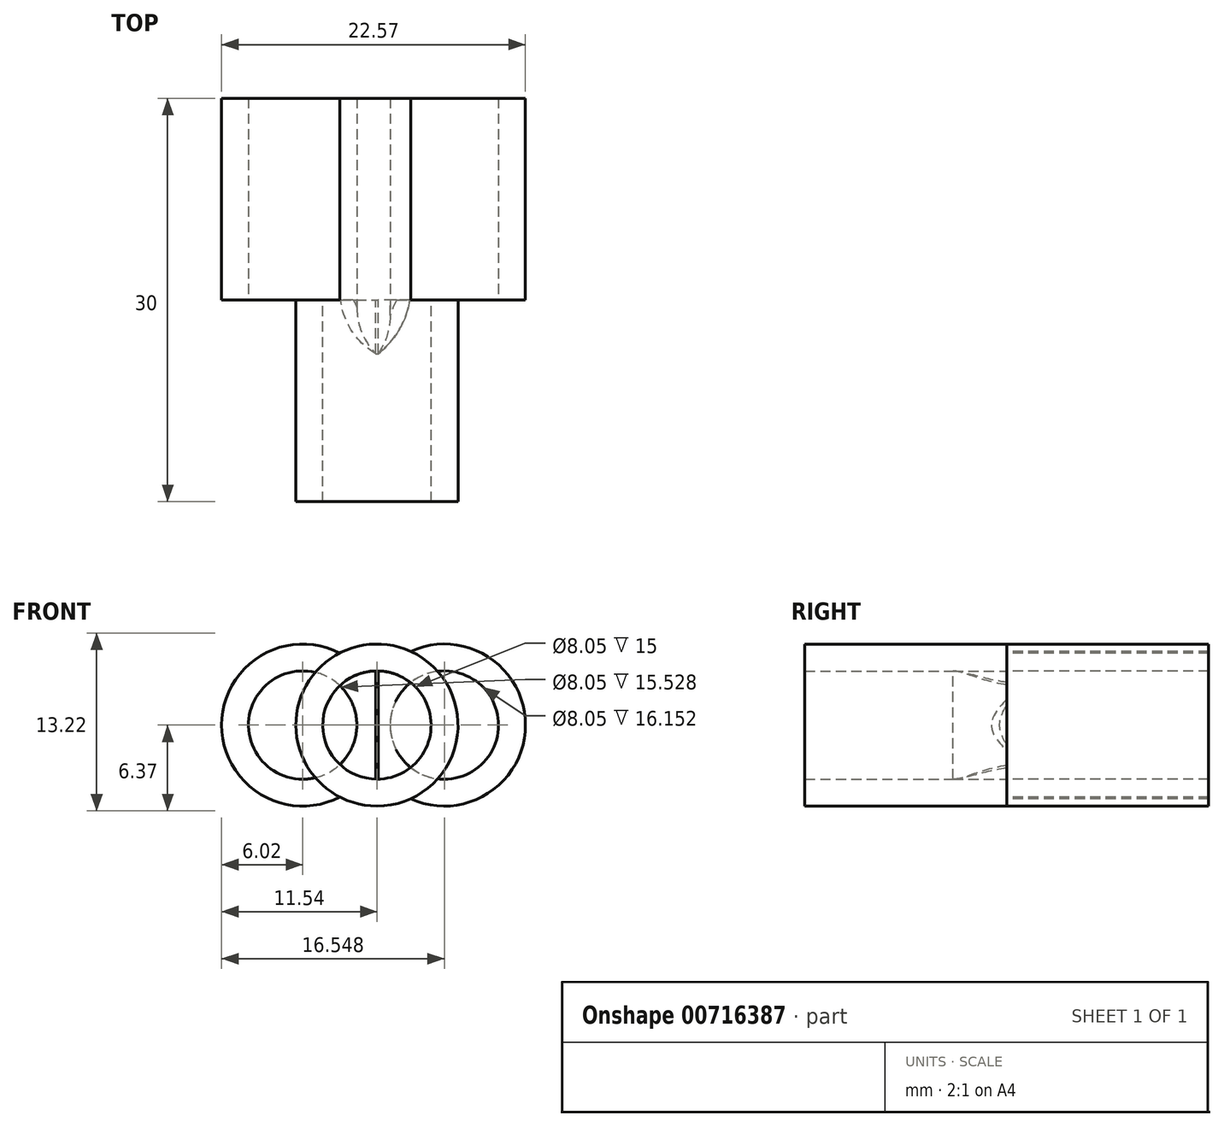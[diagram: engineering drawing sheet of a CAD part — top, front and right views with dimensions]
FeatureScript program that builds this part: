
annotation { "Feature Type Name" : "Feature", "Feature Type Description" : "" }
export const myFeature = defineFeature(function(context is Context, id is Id, definition is map)
    precondition{}
    {
        {
            var Q0;
            Q0=qCreatedBy(makeId("Front.planeOp"),FACE);
            var sketch = newSketch(context, id + "F0", { "sketchPlane" : qUnion([Q0])});
            skCircle(sketch, "E0", {"center": v(5.52, 0) * mm, "radius": 4.03 * mm});
            skCircle(sketch, "E1", {"center": v(5.52, 0) * mm, "radius": 6.03 * mm});
            skSolve(sketch);
        }
        {
            var Q0;
            Q0 = qSketchRegion(id + "F0", true);
            extrude(context, id + "F1", {"entities" : qUnion([Q0]), "depth" : 15 * mm, "offsetDistance" : 25 * mm});
        }
        {
            var Q0;
            Q0=qCreatedBy(makeId("Front.planeOp"),FACE);
            var sketch = newSketch(context, id + "F2", { "sketchPlane" : qUnion([Q0])});
            skCircle(sketch, "E2", {"center": v(10.53, 0) * mm, "radius": 6.03 * mm});
            skCircle(sketch, "E3", {"center": v(0, 0) * mm, "radius": 6.03 * mm});
            skCircle(sketch, "E4", {"center": v(10.53, 0) * mm, "radius": 4.03 * mm});
            skCircle(sketch, "E5", {"center": v(0, 0) * mm, "radius": 4.03 * mm});
            skSolve(sketch);
        }
        {
            var Q0;
            Q0=makeQuery(id+"F2.imprint","IMPRINT",FACE,{"disambiguationData":[TD([[makeQuery(id+"F2.imprint","IMPRINT",EDGE,{"derivedFrom":sQuery(id+"F2.wireOp",EDGE,"E5")}),-1.0]])]});
            var Q1;
            Q1=makeQuery(id+"F2.imprint","IMPRINT",FACE,{"disambiguationData":[TD([[makeQuery(id+"F2.imprint","IMPRINT",EDGE,{"derivedFrom":sQuery(id+"F2.wireOp",EDGE,"E4")}),-1.0]])]});
            extrude(context, id + "F3", {"entities" : qUnion([Q0, Q1]), "oppositeDirection" : true, "depth" : 15 * mm, "offsetDistance" : 25 * mm});
        }
        {
            var Q0;
            Q0=makeQuery(id+"F0.imprint","IMPRINT",FACE,{"disambiguationData":[TD([[makeQuery(id+"F0.imprint","IMPRINT",EDGE,{"derivedFrom":sQuery(id+"F0.wireOp",EDGE,"E0")}),1.0]])]});
            var sketch = newSketch(context, id + "F4", { "sketchPlane" : qUnion([Q0])});
            skArc(sketch, "E6.0", {"start": v(6.37, 4.36) * mm, "mid": v(7.15, 4.99) * mm, "end": v(8.02, 5.48) * mm});
            skArc(sketch, "E7.0", {"start": v(4.36, -4.16) * mm, "mid": v(6.03, 0) * mm, "end": v(4.36, 4.16) * mm});
            skArc(sketch, "E8.0", {"start": v(8.02, 5.48) * mm, "mid": v(5.38, 6.02) * mm, "end": v(2.76, 5.36) * mm});
            skArc(sketch, "E9.0", {"start": v(2.76, -5.36) * mm, "mid": v(6.03, 0) * mm, "end": v(2.76, 5.36) * mm});
            skArc(sketch, "E10.trimOffspring", {"start": v(2.76, -5.36) * mm, "mid": v(5.38, -6.02) * mm, "end": v(8.02, -5.48) * mm});
            skArc(sketch, "E11.0", {"start": v(5.26, 2.93) * mm, "mid": v(4.5, 0) * mm, "end": v(5.26, -2.93) * mm});
            skArc(sketch, "E12.0.0", {"start": v(5.26, 2.93) * mm, "mid": v(6.44, 4.43) * mm, "end": v(8.02, 5.48) * mm});
            skArc(sketch, "E12.0.1", {"start": v(5.26, -2.93) * mm, "mid": v(6.03, 0) * mm, "end": v(5.26, 2.93) * mm});
            skArc(sketch, "E13.0.1", {"start": v(5.26, -2.93) * mm, "mid": v(4.2, -4.33) * mm, "end": v(2.76, -5.36) * mm});
            skArc(sketch, "E14.trimOffspring", {"start": v(2.76, 5.36) * mm, "mid": v(4.2, 4.33) * mm, "end": v(5.26, 2.93) * mm});
            skArc(sketch, "E15.trimOffspring", {"start": v(8.02, -5.48) * mm, "mid": v(6.44, -4.43) * mm, "end": v(5.26, -2.93) * mm});
            skArc(sketch, "E16.trimOffspring", {"start": v(8.02, -5.48) * mm, "mid": v(7.15, -4.99) * mm, "end": v(6.37, -4.36) * mm});
            skSolve(sketch);
        }
        {
            var Q0;
            Q0 = qSketchRegion(id + "F4", true);
            extrude(context, id + "F5", {"entities" : qUnion([Q0]), "operationType" : NewBodyOperationType.ADD, "depth" : -15 * mm, "offsetDistance" : 25 * mm});
        }
        {
            var Q0;
            Q0=makeQuery(id+"F0.imprint","IMPRINT",FACE,{"disambiguationData":[TD([[makeQuery(id+"F0.imprint","IMPRINT",EDGE,{"derivedFrom":sQuery(id+"F0.wireOp",EDGE,"E0")}),1.0]])]});
            var sketch = newSketch(context, id + "F6", { "sketchPlane" : qUnion([Q0])});
            skArc(sketch, "E17.0", {"start": v(5.43, -4.02) * mm, "mid": v(5.52, -4.03) * mm, "end": v(5.61, -4.02) * mm});
            skPoint(sketch, "E18.0", {"position": v(5.61, 3.48) * mm});
            skArc(sketch, "E19.0.0", {"start": v(5.61, 4.02) * mm, "mid": v(5.1, 4) * mm, "end": v(4.58, 3.91) * mm});
            skPoint(sketch, "E20.0", {"position": v(5.61, -3.48) * mm});
            skPoint(sketch, "E21.0.end.orphan", {"position": v(5.26, 2.93) * mm});
            skPoint(sketch, "E22.0.start.orphan", {"position": v(5.26, -2.93) * mm});
            skLineSegment(sketch, "E23", {"start": v(5.61, -4.02) * mm, "end": v(5.61, 4.02) * mm});
            skLineSegment(sketch, "E24", {"start": v(5.43, -4.02) * mm, "end": v(5.43, 4.02) * mm});
            skSolve(sketch);
        }
        {
            var Q0;
            Q0 = qSketchRegion(id + "F6", true);
            extrude(context, id + "F7", {"entities" : qUnion([Q0]), "depth" : 4 * mm, "offsetDistance" : 25 * mm});
        }
        {
            var Q0;
            Q0=qCreatedBy(makeId("Front.planeOp"),FACE);
            var sketch = newSketch(context, id + "F8", { "sketchPlane" : qUnion([Q0])});
            skArc(sketch, "E25.0.0", {"start": v(8.02, 3.15) * mm, "mid": v(6.89, 3.79) * mm, "end": v(5.61, 4.02) * mm});
            skArc(sketch, "E26.0", {"start": v(8.02, 3.15) * mm, "mid": v(6.5, 0) * mm, "end": v(8.02, -3.15) * mm});
            skLineSegment(sketch, "E27.0", {"start": v(5.61, -4.02) * mm, "end": v(5.61, 4.02) * mm});
            skArc(sketch, "E28.trimOffspring", {"start": v(5.61, -4.02) * mm, "mid": v(6.89, -3.79) * mm, "end": v(8.02, -3.15) * mm});
            skSolve(sketch);
        }
        {
            var Q0;
            Q0 = qSketchRegion(id + "F8", true);
            extrude(context, id + "F9", {"entities" : qUnion([Q0]), "depth" : 4 * mm, "offsetDistance" : 25 * mm});
        }
        {
            var Q0;
            Q0=makeQuery(id+"F9.opExtrude","CAP_EDGE",EDGE,{"disambiguationData":[OSD([sQuery(id+"F8.wireOp",EDGE,"E26.0")])],"isStart":false});
            fillet(context, id + "F10", {"entities" : qUnion([Q0]), "radius" : 5 * mm, "tangentPropagation" : true, "allowEdgeOverflow" : false});
        }
        {
            var Q0;
            Q0=makeQuery(id+"F0.imprint","IMPRINT",FACE,{"disambiguationData":[TD([[makeQuery(id+"F0.imprint","IMPRINT",EDGE,{"derivedFrom":sQuery(id+"F0.wireOp",EDGE,"E0")}),1.0]])]});
            var sketch = newSketch(context, id + "F11", { "sketchPlane" : qUnion([Q0])});
            skArc(sketch, "E29.0", {"start": v(2.76, -2.93) * mm, "mid": v(4.03, 0) * mm, "end": v(2.76, 2.93) * mm});
            skArc(sketch, "E30.0", {"start": v(2.76, -2.93) * mm, "mid": v(4, -3.72) * mm, "end": v(5.43, -4.02) * mm});
            skArc(sketch, "E31.0.0", {"start": v(5.43, 4.02) * mm, "mid": v(4, 3.72) * mm, "end": v(2.76, 2.93) * mm});
            skLineSegment(sketch, "E32.0", {"start": v(5.43, -4.02) * mm, "end": v(5.43, 4.02) * mm});
            skSolve(sketch);
        }
        {
            var Q0;
            Q0 = qSketchRegion(id + "F11", true);
            extrude(context, id + "F12", {"entities" : qUnion([Q0]), "depth" : 4 * mm, "offsetDistance" : 25 * mm});
        }
        {
            var Q0;
            Q0=makeQuery(id+"F12.opExtrude","CAP_EDGE",EDGE,{"disambiguationData":[OSD([sQuery(id+"F11.wireOp",EDGE,"E29.0")])],"isStart":false});
            fillet(context, id + "F13", {"entities" : qUnion([Q0]), "radius" : 5 * mm, "tangentPropagation" : true, "allowEdgeOverflow" : false});
        }
    });
